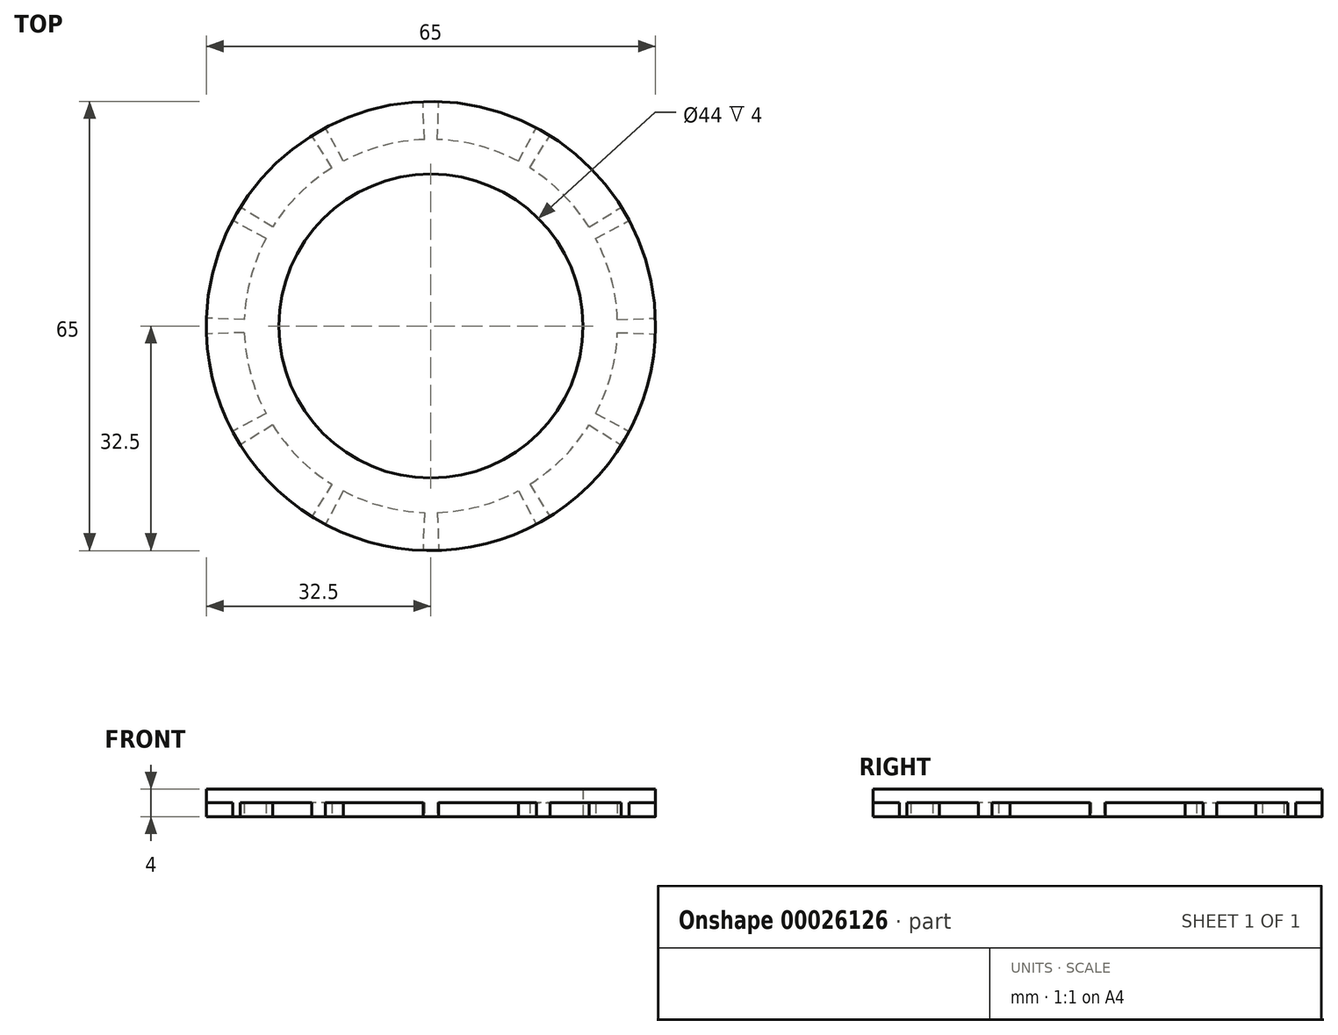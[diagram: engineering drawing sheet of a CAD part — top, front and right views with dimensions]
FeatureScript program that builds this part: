
annotation { "Feature Type Name" : "Feature", "Feature Type Description" : "" }
export const myFeature = defineFeature(function(context is Context, id is Id, definition is map)
    precondition{}
    {
        {
            var Q0;
            Q0=qCreatedBy(makeId("Top.planeOp"),FACE);
            var sketch = newSketch(context, id + "F0", { "sketchPlane" : qUnion([Q0])});
            skCircle(sketch, "E0", {"center": v(0, 0) * mm, "radius": 22 * mm});
            skArc(sketch, "E1", {"start": v(-32.48, -1.13) * mm, "mid": v(-31.4, -8.41) * mm, "end": v(-28.7, -15.26) * mm});
            skArc(sketch, "E2", {"start": v(-26.98, -0.94) * mm, "mid": v(-26.08, -6.99) * mm, "end": v(-23.84, -12.68) * mm});
            skLineSegment(sketch, "E3", {"start": v(0, 0) * mm, "end": v(-32.5, 0) * mm, "construction": true});
            skLineSegment(sketch, "E4", {"start": v(0, 0) * mm, "end": v(-21.99, 0.77) * mm, "construction": true});
            skLineSegment(sketch, "E5.MirrorCS", {"start": v(0, 0) * mm, "end": v(-21.99, -0.77) * mm, "construction": true});
            skLineSegment(sketch, "E6.1.0", {"start": v(0, 0) * mm, "end": v(-18.66, -11.66) * mm, "construction": true});
            skLineSegment(sketch, "E6.1.1", {"start": v(0, 0) * mm, "end": v(-28.15, -16.25) * mm, "construction": true});
            skLineSegment(sketch, "E6.1.2", {"start": v(0, 0) * mm, "end": v(-19.42, -10.33) * mm, "construction": true});
            skLineSegment(sketch, "E6.2.0", {"start": v(0, 0) * mm, "end": v(-10.33, -19.42) * mm, "construction": true});
            skLineSegment(sketch, "E6.2.1", {"start": v(0, 0) * mm, "end": v(-16.25, -28.15) * mm, "construction": true});
            skLineSegment(sketch, "E6.2.2", {"start": v(0, 0) * mm, "end": v(-11.66, -18.66) * mm, "construction": true});
            skLineSegment(sketch, "E6.3.0", {"start": v(0, 0) * mm, "end": v(0.77, -21.99) * mm, "construction": true});
            skLineSegment(sketch, "E6.3.1", {"start": v(0, 0) * mm, "end": v(0, -32.5) * mm, "construction": true});
            skLineSegment(sketch, "E6.3.2", {"start": v(0, 0) * mm, "end": v(-0.77, -21.99) * mm, "construction": true});
            skLineSegment(sketch, "E6.4.0", {"start": v(0, 0) * mm, "end": v(11.66, -18.66) * mm, "construction": true});
            skLineSegment(sketch, "E6.4.1", {"start": v(0, 0) * mm, "end": v(16.25, -28.15) * mm, "construction": true});
            skLineSegment(sketch, "E6.4.2", {"start": v(0, 0) * mm, "end": v(10.33, -19.42) * mm, "construction": true});
            skLineSegment(sketch, "E6.5.0", {"start": v(0, 0) * mm, "end": v(19.42, -10.33) * mm, "construction": true});
            skLineSegment(sketch, "E6.5.1", {"start": v(0, 0) * mm, "end": v(28.15, -16.25) * mm, "construction": true});
            skLineSegment(sketch, "E6.5.2", {"start": v(0, 0) * mm, "end": v(18.66, -11.66) * mm, "construction": true});
            skLineSegment(sketch, "E6.6.0", {"start": v(0, 0) * mm, "end": v(21.99, 0.77) * mm, "construction": true});
            skLineSegment(sketch, "E6.6.1", {"start": v(0, 0) * mm, "end": v(32.5, 0) * mm, "construction": true});
            skLineSegment(sketch, "E6.6.2", {"start": v(0, 0) * mm, "end": v(21.99, -0.77) * mm, "construction": true});
            skLineSegment(sketch, "E6.7.0", {"start": v(0, 0) * mm, "end": v(18.66, 11.66) * mm, "construction": true});
            skLineSegment(sketch, "E6.7.1", {"start": v(0, 0) * mm, "end": v(28.15, 16.25) * mm, "construction": true});
            skLineSegment(sketch, "E6.7.2", {"start": v(0, 0) * mm, "end": v(19.42, 10.33) * mm, "construction": true});
            skLineSegment(sketch, "E6.8.0", {"start": v(0, 0) * mm, "end": v(10.33, 19.42) * mm, "construction": true});
            skLineSegment(sketch, "E6.8.1", {"start": v(0, 0) * mm, "end": v(16.25, 28.15) * mm, "construction": true});
            skLineSegment(sketch, "E6.8.2", {"start": v(0, 0) * mm, "end": v(11.66, 18.66) * mm, "construction": true});
            skLineSegment(sketch, "E6.9.0", {"start": v(0, 0) * mm, "end": v(-0.77, 21.99) * mm, "construction": true});
            skLineSegment(sketch, "E6.9.1", {"start": v(0, 0) * mm, "end": v(0, 32.5) * mm, "construction": true});
            skLineSegment(sketch, "E6.9.2", {"start": v(0, 0) * mm, "end": v(0.77, 21.99) * mm, "construction": true});
            skLineSegment(sketch, "E6.10.0", {"start": v(0, 0) * mm, "end": v(-11.66, 18.66) * mm, "construction": true});
            skLineSegment(sketch, "E6.10.1", {"start": v(0, 0) * mm, "end": v(-16.25, 28.15) * mm, "construction": true});
            skLineSegment(sketch, "E6.10.2", {"start": v(0, 0) * mm, "end": v(-10.33, 19.42) * mm, "construction": true});
            skLineSegment(sketch, "E6.11.0", {"start": v(0, 0) * mm, "end": v(-19.42, 10.33) * mm, "construction": true});
            skLineSegment(sketch, "E6.11.1", {"start": v(0, 0) * mm, "end": v(-28.15, 16.25) * mm, "construction": true});
            skLineSegment(sketch, "E6.11.2", {"start": v(0, 0) * mm, "end": v(-18.66, 11.66) * mm, "construction": true});
            skLineSegment(sketch, "E7.trimOffspring", {"start": v(-23.84, 12.68) * mm, "end": v(-28.7, 15.26) * mm});
            skLineSegment(sketch, "E8.trimOffspring", {"start": v(-22.9, 14.3) * mm, "end": v(-27.56, 17.22) * mm});
            skLineSegment(sketch, "E9.trimOffspring", {"start": v(-14.3, 22.9) * mm, "end": v(-17.22, 27.56) * mm});
            skLineSegment(sketch, "E10.trimOffspring", {"start": v(-12.68, 23.84) * mm, "end": v(-15.26, 28.7) * mm});
            skLineSegment(sketch, "E11.trimOffspring", {"start": v(-0.94, 26.98) * mm, "end": v(-1.13, 32.48) * mm});
            skLineSegment(sketch, "E12.trimOffspring", {"start": v(0.94, 26.98) * mm, "end": v(1.13, 32.48) * mm});
            skLineSegment(sketch, "E13.trimOffspring", {"start": v(12.68, 23.84) * mm, "end": v(15.26, 28.7) * mm});
            skLineSegment(sketch, "E14.trimOffspring", {"start": v(14.3, 22.9) * mm, "end": v(17.22, 27.56) * mm});
            skLineSegment(sketch, "E15.trimOffspring", {"start": v(22.9, 14.3) * mm, "end": v(27.56, 17.22) * mm});
            skLineSegment(sketch, "E16.trimOffspring", {"start": v(23.84, 12.68) * mm, "end": v(28.7, 15.26) * mm});
            skLineSegment(sketch, "E17.trimOffspring", {"start": v(26.98, 0.94) * mm, "end": v(32.48, 1.13) * mm});
            skLineSegment(sketch, "E18.trimOffspring", {"start": v(26.98, -0.94) * mm, "end": v(32.48, -1.13) * mm});
            skLineSegment(sketch, "E19.trimOffspring", {"start": v(23.84, -12.68) * mm, "end": v(28.7, -15.26) * mm});
            skLineSegment(sketch, "E20.trimOffspring", {"start": v(22.9, -14.3) * mm, "end": v(27.56, -17.22) * mm});
            skLineSegment(sketch, "E21.trimOffspring", {"start": v(14.3, -22.9) * mm, "end": v(17.22, -27.56) * mm});
            skLineSegment(sketch, "E22.trimOffspring", {"start": v(12.68, -23.84) * mm, "end": v(15.26, -28.7) * mm});
            skLineSegment(sketch, "E23.trimOffspring", {"start": v(0.94, -26.98) * mm, "end": v(1.13, -32.48) * mm});
            skLineSegment(sketch, "E24.trimOffspring", {"start": v(-0.94, -26.98) * mm, "end": v(-1.13, -32.48) * mm});
            skLineSegment(sketch, "E25.trimOffspring", {"start": v(-12.68, -23.84) * mm, "end": v(-15.26, -28.7) * mm});
            skLineSegment(sketch, "E26.trimOffspring", {"start": v(-14.3, -22.9) * mm, "end": v(-17.22, -27.56) * mm});
            skLineSegment(sketch, "E27.trimOffspring", {"start": v(-22.9, -14.3) * mm, "end": v(-27.56, -17.22) * mm});
            skLineSegment(sketch, "E28.trimOffspring", {"start": v(-23.84, -12.68) * mm, "end": v(-28.7, -15.26) * mm});
            skLineSegment(sketch, "E29.trimOffspring", {"start": v(-26.98, -0.94) * mm, "end": v(-32.48, -1.13) * mm});
            skLineSegment(sketch, "E30.trimOffspring", {"start": v(-26.98, 0.94) * mm, "end": v(-32.48, 1.13) * mm});
            skArc(sketch, "E31.trimOffspring", {"start": v(-23.84, 12.68) * mm, "mid": v(-26.08, 6.99) * mm, "end": v(-26.98, 0.94) * mm});
            skArc(sketch, "E32.trimOffspring", {"start": v(-28.7, 15.26) * mm, "mid": v(-31.4, 8.41) * mm, "end": v(-32.48, 1.13) * mm});
            skArc(sketch, "E33.trimOffspring", {"start": v(-14.3, 22.9) * mm, "mid": v(-19.1, 19.1) * mm, "end": v(-22.9, 14.3) * mm});
            skArc(sketch, "E34.trimOffspring", {"start": v(-17.22, 27.56) * mm, "mid": v(-22.98, 22.98) * mm, "end": v(-27.56, 17.22) * mm});
            skArc(sketch, "E35.trimOffspring", {"start": v(-1.13, 32.48) * mm, "mid": v(-8.41, 31.4) * mm, "end": v(-15.26, 28.7) * mm});
            skArc(sketch, "E36.trimOffspring", {"start": v(-0.94, 26.98) * mm, "mid": v(-6.99, 26.08) * mm, "end": v(-12.68, 23.84) * mm});
            skArc(sketch, "E37.trimOffspring", {"start": v(15.26, 28.7) * mm, "mid": v(8.41, 31.4) * mm, "end": v(1.13, 32.48) * mm});
            skArc(sketch, "E38.trimOffspring", {"start": v(12.68, 23.84) * mm, "mid": v(6.99, 26.08) * mm, "end": v(0.94, 26.98) * mm});
            skArc(sketch, "E39.trimOffspring", {"start": v(27.56, 17.22) * mm, "mid": v(22.98, 22.98) * mm, "end": v(17.22, 27.56) * mm});
            skArc(sketch, "E40.trimOffspring", {"start": v(22.9, 14.3) * mm, "mid": v(19.1, 19.1) * mm, "end": v(14.3, 22.9) * mm});
            skArc(sketch, "E41.trimOffspring", {"start": v(32.48, 1.13) * mm, "mid": v(31.4, 8.41) * mm, "end": v(28.7, 15.26) * mm});
            skArc(sketch, "E42.trimOffspring", {"start": v(26.98, 0.94) * mm, "mid": v(26.08, 6.99) * mm, "end": v(23.84, 12.68) * mm});
            skArc(sketch, "E43.trimOffspring", {"start": v(23.84, -12.68) * mm, "mid": v(26.08, -6.99) * mm, "end": v(26.98, -0.94) * mm});
            skArc(sketch, "E44.trimOffspring", {"start": v(28.7, -15.26) * mm, "mid": v(31.4, -8.41) * mm, "end": v(32.48, -1.13) * mm});
            skArc(sketch, "E45.trimOffspring", {"start": v(-22.9, -14.3) * mm, "mid": v(-19.1, -19.1) * mm, "end": v(-14.3, -22.9) * mm});
            skArc(sketch, "E46.trimOffspring", {"start": v(-27.56, -17.22) * mm, "mid": v(-22.98, -22.98) * mm, "end": v(-17.22, -27.56) * mm});
            skArc(sketch, "E47.trimOffspring", {"start": v(-15.26, -28.7) * mm, "mid": v(-8.41, -31.4) * mm, "end": v(-1.13, -32.48) * mm});
            skArc(sketch, "E48.trimOffspring", {"start": v(-12.68, -23.84) * mm, "mid": v(-6.99, -26.08) * mm, "end": v(-0.94, -26.98) * mm});
            skArc(sketch, "E49.trimOffspring", {"start": v(0.94, -26.98) * mm, "mid": v(6.99, -26.08) * mm, "end": v(12.68, -23.84) * mm});
            skArc(sketch, "E50.trimOffspring", {"start": v(1.13, -32.48) * mm, "mid": v(8.41, -31.4) * mm, "end": v(15.26, -28.7) * mm});
            skArc(sketch, "E51.trimOffspring", {"start": v(14.3, -22.9) * mm, "mid": v(19.1, -19.1) * mm, "end": v(22.9, -14.3) * mm});
            skArc(sketch, "E52.trimOffspring", {"start": v(17.22, -27.56) * mm, "mid": v(22.98, -22.98) * mm, "end": v(27.56, -17.22) * mm});
            skCircle(sketch, "E53", {"center": v(0, 0) * mm, "radius": 32.5 * mm});
            skSolve(sketch);
        }
        {
            var Q0;
            Q0=makeQuery(id+"F0.imprint","IMPRINT",FACE,{"disambiguationData":[TD([[makeQuery(id+"F0.imprint","IMPRINT",EDGE,{"derivedFrom":sQuery(id+"F0.wireOp",EDGE,"E0")}),-1.0]])]});
            var Q1;
            {var subQ1=sQuery(id+"F0.wireOp",EDGE,"E8.trimOffspring");Q1=makeQuery(id+"F0.imprint","IMPRINT",FACE,{"disambiguationData":[TD([[makeQuery(id+"F0.imprint","IMPRINT",EDGE,{"derivedFrom":subQ1}),-1.0]])]});}
            var Q2;
            {var subQ1=sQuery(id+"F0.wireOp",EDGE,"E9.trimOffspring");Q2=makeQuery(id+"F0.imprint","IMPRINT",FACE,{"disambiguationData":[TD([[makeQuery(id+"F0.imprint","IMPRINT",EDGE,{"derivedFrom":subQ1}),-1.0]])]});}
            var Q3;
            {var subQ2=sQuery(id+"F0.wireOp",EDGE,"E10.trimOffspring");Q3=makeQuery(id+"F0.imprint","IMPRINT",FACE,{"disambiguationData":[TD([[makeQuery(id+"F0.imprint","IMPRINT",EDGE,{"derivedFrom":subQ2}),-1.0]])]});}
            var Q4;
            {var subQ1=sQuery(id+"F0.wireOp",EDGE,"E11.trimOffspring");Q4=makeQuery(id+"F0.imprint","IMPRINT",FACE,{"disambiguationData":[TD([[makeQuery(id+"F0.imprint","IMPRINT",EDGE,{"derivedFrom":subQ1}),-1.0]])]});}
            var Q5;
            {var subQ1=sQuery(id+"F0.wireOp",EDGE,"E12.trimOffspring");Q5=makeQuery(id+"F0.imprint","IMPRINT",FACE,{"disambiguationData":[TD([[makeQuery(id+"F0.imprint","IMPRINT",EDGE,{"derivedFrom":subQ1}),-1.0]])]});}
            var Q6;
            {var subQ1=sQuery(id+"F0.wireOp",EDGE,"E13.trimOffspring");Q6=makeQuery(id+"F0.imprint","IMPRINT",FACE,{"disambiguationData":[TD([[makeQuery(id+"F0.imprint","IMPRINT",EDGE,{"derivedFrom":subQ1}),-1.0]])]});}
            var Q7;
            {var subQ0=sQuery(id+"F0.wireOp",EDGE,"E14.trimOffspring");Q7=makeQuery(id+"F0.imprint","IMPRINT",FACE,{"disambiguationData":[TD([[makeQuery(id+"F0.imprint","IMPRINT",EDGE,{"derivedFrom":subQ0}),-1.0]])]});}
            var Q8;
            {var subQ1=sQuery(id+"F0.wireOp",EDGE,"E15.trimOffspring");Q8=makeQuery(id+"F0.imprint","IMPRINT",FACE,{"disambiguationData":[TD([[makeQuery(id+"F0.imprint","IMPRINT",EDGE,{"derivedFrom":subQ1}),-1.0]])]});}
            var Q9;
            {var subQ1=sQuery(id+"F0.wireOp",EDGE,"E16.trimOffspring");Q9=makeQuery(id+"F0.imprint","IMPRINT",FACE,{"disambiguationData":[TD([[makeQuery(id+"F0.imprint","IMPRINT",EDGE,{"derivedFrom":subQ1}),-1.0]])]});}
            var Q10;
            {var subQ1=sQuery(id+"F0.wireOp",EDGE,"E17.trimOffspring");Q10=makeQuery(id+"F0.imprint","IMPRINT",FACE,{"disambiguationData":[TD([[makeQuery(id+"F0.imprint","IMPRINT",EDGE,{"derivedFrom":subQ1}),-1.0]])]});}
            var Q11;
            {var subQ0=sQuery(id+"F0.wireOp",EDGE,"E18.trimOffspring");Q11=makeQuery(id+"F0.imprint","IMPRINT",FACE,{"disambiguationData":[TD([[makeQuery(id+"F0.imprint","IMPRINT",EDGE,{"derivedFrom":subQ0}),-1.0]])]});}
            var Q12;
            {var subQ1=sQuery(id+"F0.wireOp",EDGE,"E19.trimOffspring");Q12=makeQuery(id+"F0.imprint","IMPRINT",FACE,{"disambiguationData":[TD([[makeQuery(id+"F0.imprint","IMPRINT",EDGE,{"derivedFrom":subQ1}),-1.0]])]});}
            var Q13;
            {var subQ1=sQuery(id+"F0.wireOp",EDGE,"E20.trimOffspring");Q13=makeQuery(id+"F0.imprint","IMPRINT",FACE,{"disambiguationData":[TD([[makeQuery(id+"F0.imprint","IMPRINT",EDGE,{"derivedFrom":subQ1}),-1.0]])]});}
            var Q14;
            {var subQ0=sQuery(id+"F0.wireOp",EDGE,"E21.trimOffspring");Q14=makeQuery(id+"F0.imprint","IMPRINT",FACE,{"disambiguationData":[TD([[makeQuery(id+"F0.imprint","IMPRINT",EDGE,{"derivedFrom":subQ0}),-1.0]])]});}
            var Q15;
            {var subQ2=sQuery(id+"F0.wireOp",EDGE,"E22.trimOffspring");Q15=makeQuery(id+"F0.imprint","IMPRINT",FACE,{"disambiguationData":[TD([[makeQuery(id+"F0.imprint","IMPRINT",EDGE,{"derivedFrom":subQ2}),-1.0]])]});}
            var Q16;
            {var subQ1=sQuery(id+"F0.wireOp",EDGE,"E23.trimOffspring");Q16=makeQuery(id+"F0.imprint","IMPRINT",FACE,{"disambiguationData":[TD([[makeQuery(id+"F0.imprint","IMPRINT",EDGE,{"derivedFrom":subQ1}),-1.0]])]});}
            var Q17;
            {var subQ1=sQuery(id+"F0.wireOp",EDGE,"E24.trimOffspring");Q17=makeQuery(id+"F0.imprint","IMPRINT",FACE,{"disambiguationData":[TD([[makeQuery(id+"F0.imprint","IMPRINT",EDGE,{"derivedFrom":subQ1}),-1.0]])]});}
            var Q18;
            {var subQ0=sQuery(id+"F0.wireOp",EDGE,"E25.trimOffspring");Q18=makeQuery(id+"F0.imprint","IMPRINT",FACE,{"disambiguationData":[TD([[makeQuery(id+"F0.imprint","IMPRINT",EDGE,{"derivedFrom":subQ0}),-1.0]])]});}
            var Q19;
            {var subQ1=sQuery(id+"F0.wireOp",EDGE,"E26.trimOffspring");Q19=makeQuery(id+"F0.imprint","IMPRINT",FACE,{"disambiguationData":[TD([[makeQuery(id+"F0.imprint","IMPRINT",EDGE,{"derivedFrom":subQ1}),-1.0]])]});}
            var Q20;
            {var subQ1=sQuery(id+"F0.wireOp",EDGE,"E27.trimOffspring");Q20=makeQuery(id+"F0.imprint","IMPRINT",FACE,{"disambiguationData":[TD([[makeQuery(id+"F0.imprint","IMPRINT",EDGE,{"derivedFrom":subQ1}),-1.0]])]});}
            var Q21;
            {var subQ1=sQuery(id+"F0.wireOp",EDGE,"E28.trimOffspring");Q21=makeQuery(id+"F0.imprint","IMPRINT",FACE,{"disambiguationData":[TD([[makeQuery(id+"F0.imprint","IMPRINT",EDGE,{"derivedFrom":subQ1}),-1.0]])]});}
            var Q22;
            {var subQ0=sQuery(id+"F0.wireOp",EDGE,"E29.trimOffspring");Q22=makeQuery(id+"F0.imprint","IMPRINT",FACE,{"disambiguationData":[TD([[makeQuery(id+"F0.imprint","IMPRINT",EDGE,{"derivedFrom":subQ0}),-1.0]])]});}
            var Q23;
            {var subQ1=sQuery(id+"F0.wireOp",EDGE,"E7.trimOffspring");Q23=makeQuery(id+"F0.imprint","IMPRINT",FACE,{"disambiguationData":[TD([[makeQuery(id+"F0.imprint","IMPRINT",EDGE,{"derivedFrom":subQ1}),1.0]])]});}
            var Q24;
            {var subQ1=sQuery(id+"F0.wireOp",EDGE,"E7.trimOffspring");Q24=makeQuery(id+"F0.imprint","IMPRINT",FACE,{"disambiguationData":[TD([[makeQuery(id+"F0.imprint","IMPRINT",EDGE,{"derivedFrom":subQ1}),-1.0]])]});}
            extrude(context, id + "F1", {"entities" : qUnion([Q0, Q1, Q2, Q3, Q4, Q5, Q6, Q7, Q8, Q9, Q10, Q11, Q12, Q13, Q14, Q15, Q16, Q17, Q18, Q19, Q20, Q21, Q22, Q23, Q24]), "depth" : 4 * mm});
        }
        {
            var Q0;
            {var subQ2=sQuery(id+"F0.wireOp",EDGE,"E10.trimOffspring");Q0=makeQuery(id+"F0.imprint","IMPRINT",FACE,{"disambiguationData":[TD([[makeQuery(id+"F0.imprint","IMPRINT",EDGE,{"derivedFrom":subQ2}),-1.0]])]});}
            var Q1;
            {var subQ1=sQuery(id+"F0.wireOp",EDGE,"E8.trimOffspring");Q1=makeQuery(id+"F0.imprint","IMPRINT",FACE,{"disambiguationData":[TD([[makeQuery(id+"F0.imprint","IMPRINT",EDGE,{"derivedFrom":subQ1}),-1.0]])]});}
            var Q2;
            {var subQ1=sQuery(id+"F0.wireOp",EDGE,"E7.trimOffspring");Q2=makeQuery(id+"F0.imprint","IMPRINT",FACE,{"disambiguationData":[TD([[makeQuery(id+"F0.imprint","IMPRINT",EDGE,{"derivedFrom":subQ1}),1.0]])]});}
            var Q3;
            {var subQ1=sQuery(id+"F0.wireOp",EDGE,"E28.trimOffspring");Q3=makeQuery(id+"F0.imprint","IMPRINT",FACE,{"disambiguationData":[TD([[makeQuery(id+"F0.imprint","IMPRINT",EDGE,{"derivedFrom":subQ1}),-1.0]])]});}
            var Q4;
            {var subQ1=sQuery(id+"F0.wireOp",EDGE,"E26.trimOffspring");Q4=makeQuery(id+"F0.imprint","IMPRINT",FACE,{"disambiguationData":[TD([[makeQuery(id+"F0.imprint","IMPRINT",EDGE,{"derivedFrom":subQ1}),-1.0]])]});}
            var Q5;
            {var subQ1=sQuery(id+"F0.wireOp",EDGE,"E24.trimOffspring");Q5=makeQuery(id+"F0.imprint","IMPRINT",FACE,{"disambiguationData":[TD([[makeQuery(id+"F0.imprint","IMPRINT",EDGE,{"derivedFrom":subQ1}),-1.0]])]});}
            var Q6;
            {var subQ2=sQuery(id+"F0.wireOp",EDGE,"E22.trimOffspring");Q6=makeQuery(id+"F0.imprint","IMPRINT",FACE,{"disambiguationData":[TD([[makeQuery(id+"F0.imprint","IMPRINT",EDGE,{"derivedFrom":subQ2}),-1.0]])]});}
            var Q7;
            {var subQ1=sQuery(id+"F0.wireOp",EDGE,"E20.trimOffspring");Q7=makeQuery(id+"F0.imprint","IMPRINT",FACE,{"disambiguationData":[TD([[makeQuery(id+"F0.imprint","IMPRINT",EDGE,{"derivedFrom":subQ1}),-1.0]])]});}
            var Q8;
            {var subQ0=sQuery(id+"F0.wireOp",EDGE,"E18.trimOffspring");Q8=makeQuery(id+"F0.imprint","IMPRINT",FACE,{"disambiguationData":[TD([[makeQuery(id+"F0.imprint","IMPRINT",EDGE,{"derivedFrom":subQ0}),-1.0]])]});}
            var Q9;
            {var subQ1=sQuery(id+"F0.wireOp",EDGE,"E16.trimOffspring");Q9=makeQuery(id+"F0.imprint","IMPRINT",FACE,{"disambiguationData":[TD([[makeQuery(id+"F0.imprint","IMPRINT",EDGE,{"derivedFrom":subQ1}),-1.0]])]});}
            var Q10;
            {var subQ0=sQuery(id+"F0.wireOp",EDGE,"E14.trimOffspring");Q10=makeQuery(id+"F0.imprint","IMPRINT",FACE,{"disambiguationData":[TD([[makeQuery(id+"F0.imprint","IMPRINT",EDGE,{"derivedFrom":subQ0}),-1.0]])]});}
            var Q11;
            {var subQ1=sQuery(id+"F0.wireOp",EDGE,"E12.trimOffspring");Q11=makeQuery(id+"F0.imprint","IMPRINT",FACE,{"disambiguationData":[TD([[makeQuery(id+"F0.imprint","IMPRINT",EDGE,{"derivedFrom":subQ1}),-1.0]])]});}
            extrude(context, id + "F2", {"entities" : qUnion([Q0, Q1, Q2, Q3, Q4, Q5, Q6, Q7, Q8, Q9, Q10, Q11]), "operationType" : NewBodyOperationType.REMOVE, "depth" : 2 * mm});
        }
    });
